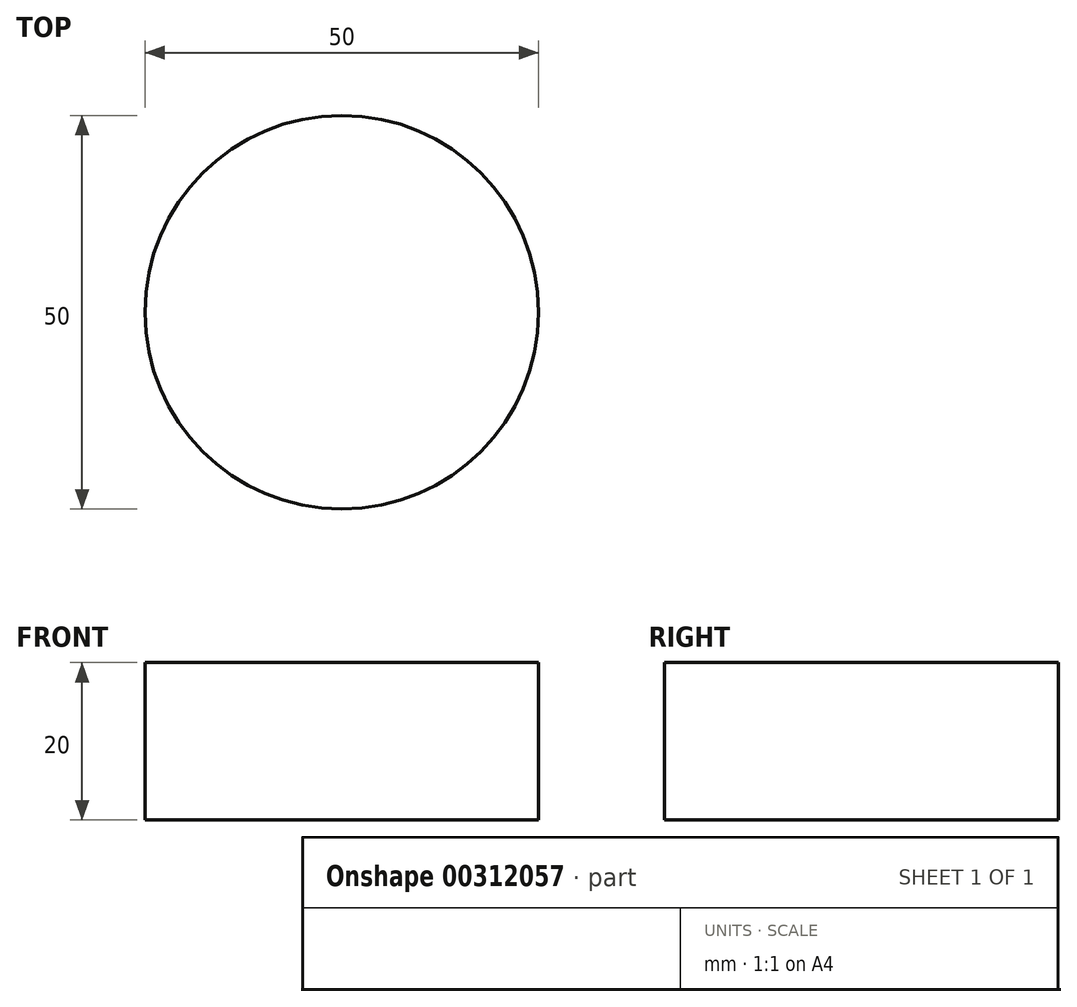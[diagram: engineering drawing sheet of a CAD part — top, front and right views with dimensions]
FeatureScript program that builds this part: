
annotation { "Feature Type Name" : "Feature", "Feature Type Description" : "" }
export const myFeature = defineFeature(function(context is Context, id is Id, definition is map)
    precondition{}
    {
        {
            var Q0;
            Q0=qCreatedBy(makeId("Top.planeOp"),FACE);
            var sketch = newSketch(context, id + "F0", { "sketchPlane" : qUnion([Q0])});
            skCircle(sketch, "E0", {"center": v(0, 0) * mm, "radius": 25 * mm});
            skSolve(sketch);
        }
        {
            var Q0;
            Q0 = qSketchRegion(id + "F0", true);
            extrude(context, id + "F1", {"entities" : qUnion([Q0]), "depth" : 20 * mm});
        }
    });
